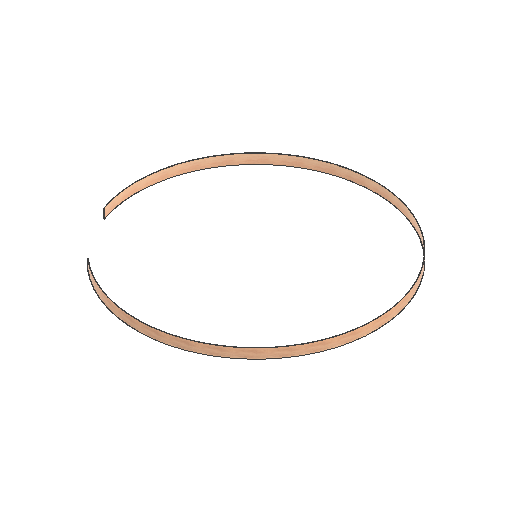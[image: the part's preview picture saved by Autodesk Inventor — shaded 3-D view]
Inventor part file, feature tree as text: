
AUTODESK INVENTOR PART (.ipt)
format: ipt  version: 2021 (Build 250183000, 183)  size: 120,320 bytes
history: native  units: mm
features: other x4, extrude x2, sketch x2, reference x2
ambient origin geometry x8: Origin, YZ Plane, XZ Plane, XY Plane, X Axis, Y Axis, Z Axis, Center Point
bodies: Solid1 (feature_tree)
feature tree (10):
  extrude  "Extrusion1"  Depth=100.0mm
  extrude  "Extrusion2"  Depth=100.0mm TaperAngle=0.0deg
  sketch  "Sketch1"  dims[d2=100.0mm d3=0.0mm d8=2437.22mm]
  sketch  "Sketch2"  dims[d9=2445.22mm d10=100.0mm d11=0.0mm]
  reference  "Reference1"
  reference  "Reference2"
  other  "Full Scale Assembly.iam"
  other  "Disc E Assembly:1"
  other  "Platform E4:1"
  other  "Platform E1:1"
